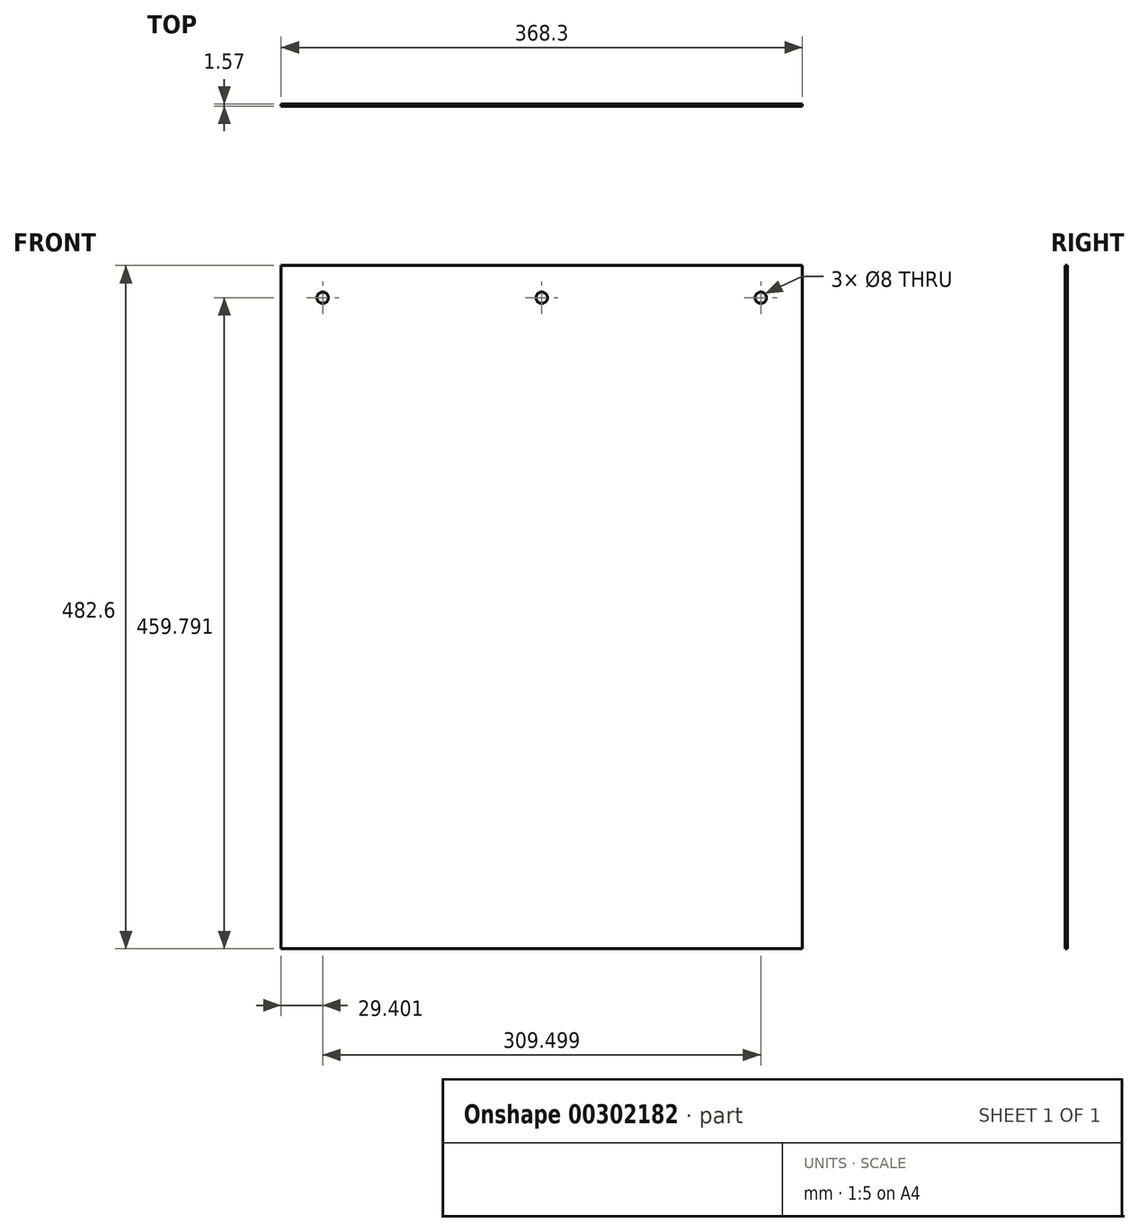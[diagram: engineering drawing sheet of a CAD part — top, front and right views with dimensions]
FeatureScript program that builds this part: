
annotation { "Feature Type Name" : "Feature", "Feature Type Description" : "" }
export const myFeature = defineFeature(function(context is Context, id is Id, definition is map)
    precondition{}
    {
        {
            var Q0;
            Q0=qCreatedBy(makeId("Front.planeOp"),FACE);
            var sketch = newSketch(context, id + "F0", { "sketchPlane" : qUnion([Q0])});
            skLineSegment(sketch, "E0.bottom", {"start": v(0, 0) * mm, "end": v(368.3, 0) * mm});
            skLineSegment(sketch, "E0.top", {"start": v(0, 482.6) * mm, "end": v(368.3, 482.6) * mm});
            skLineSegment(sketch, "E0.left", {"start": v(0, 0) * mm, "end": v(0, 482.6) * mm});
            skLineSegment(sketch, "E0.right", {"start": v(368.3, 0) * mm, "end": v(368.3, 482.6) * mm});
            skCircle(sketch, "E1", {"center": v(29.4, 459.8) * mm, "radius": 4 * mm});
            skCircle(sketch, "E2", {"center": v(184.15, 459.8) * mm, "radius": 4 * mm});
            skCircle(sketch, "E3", {"center": v(338.9, 459.8) * mm, "radius": 4 * mm});
            skSolve(sketch);
        }
        {
            var Q0;
            Q0=makeQuery(id+"F0.imprint","IMPRINT",FACE,{"disambiguationData":[TD([[makeQuery(id+"F0.imprint","IMPRINT",EDGE,{"derivedFrom":sQuery(id+"F0.wireOp",EDGE,"E0.bottom")}),1.0]])]});
            extrude(context, id + "F1", {"entities" : qUnion([Q0]), "depth" : 1.57 * mm});
        }
    });
